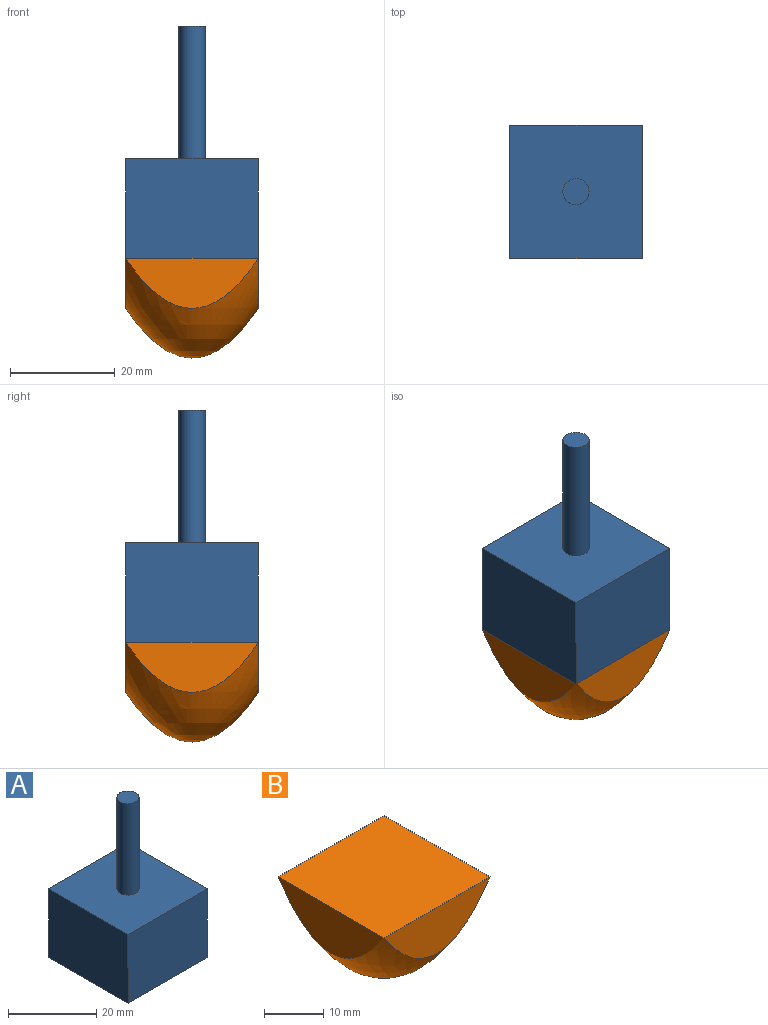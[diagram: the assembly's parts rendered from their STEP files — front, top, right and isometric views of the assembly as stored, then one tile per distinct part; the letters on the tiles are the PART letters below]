
ASSEMBLY  parts=2 mates=1
PART A: 8 faces, bbox 25.4x25.4x44.5 mm
  f0: plane 25.4x19.05mm, normal (-1,0,0), area 483.9mm2, adj f1,f3,f4,f5
  f1: plane 25.4x25.4mm, normal (0,0,-1), area 645.2mm2, adj f0,f2,f4,f5
  f2: plane 25.4x19.05mm, normal (1,0,0), area 483.9mm2, adj f1,f3,f4,f5
  f3: plane 25.4x25.4mm, normal (0,0,1), area 625.5mm2, adj f0,f2,f4,f5,f6
  f4: plane 25.4x19.05mm, normal (0,-1,0), area 483.9mm2, adj f0,f1,f2,f3
  f5: plane 25.4x19.05mm, normal (0,1,0), area 483.9mm2, adj f0,f1,f2,f3
  f6: cylinder r=2.5mm len=25.4mm, axis (0,0,-1), area 399mm2, adj f3,f7
  f7: plane 5x5mm, normal (0,0,1), area 19.6mm2, adj f6
PART B: 6 faces, bbox 35.9x35.9x19.1 mm
  f0: revolved ~35.92x35.92mm, area 1001.4mm2, adj f2,f3,f4,f5
  f1: plane 25.4x25.4mm, normal (0,0,1), area 645.2mm2, adj f2,f3,f4,f5
  f2: plane 25.4x9.53mm, normal (1,0,0), area 161.3mm2, adj f0,f1
  f3: plane 25.4x9.53mm, normal (-1,0,0), area 161.3mm2, adj f0,f1
  f4: plane 25.4x9.53mm, normal (0,-1,0), area 161.3mm2, adj f0,f1
  f5: plane 25.4x9.53mm, normal (0,1,0), area 161.3mm2, adj f0,f1
PLACE A t=(0.79,66.02,75.93)mm
PLACE B t=(13.49,53.32,56.88)mm
MATE fastened A.f6 <-> B.f1  axis (0,0,-1) through (13.49,53.32,75.93)mm
